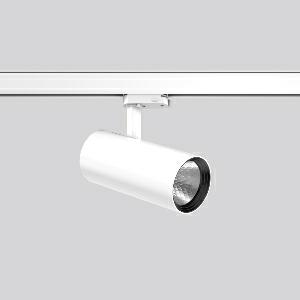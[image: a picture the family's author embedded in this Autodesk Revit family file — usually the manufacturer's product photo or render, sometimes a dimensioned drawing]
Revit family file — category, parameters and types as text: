
# Revit family: deecos_s_mini_742196_002_3_76_8a93
name_source: partatom
category: Lighting Fixtures
units: mm (PartAtom-declared; Revit-internal decimal feet)

## family parameters
Cut with Voids When Loaded = No
Host = Face
Light Source = No
Part Type = Normal
Room Calculation Point = No
Round Connector Dimension = Use Diameter
Shared = No

## types (1)
- DEECOS S mini (1 x LED Modul 935, 2500 lm, 3500)
    Apparent Load = 20 VA
    Approval mark = CE
    CIE Flux Codes = 99 100 100 100 100
    Color Rendering = 92
    Color Temperature = 3500
    Default Elevation = 1800 mm
    Description = Series: DEECOS S mini
LED surface-mounted projector in modern design with no visible cooling ribs. Housing: die-cast aluminium, powder-coated. Rotation range: 356°. Swivel range: 90°. Black plastic ring and recessed LED to prevent glare from the side. Optical assembly with reflector made of MIRO-Silver with 98% total light reflection for outstanding efficiency - can be changed without tools. Best colour rendering index Ra>90. With adapter for RZB 3-circuit DALI tracks. Suitable for Track on ceiling, Wall track. High quality converter without flickering and stroboscopic effect. The following accessories can be mounted without use of tools: interchangeable lenses, decorative glasses, honeycomb louvre, clear and frosted diffusers, white interchangeable plastic ring. 
Colour: traffic white, matt (RAL 9016)
Diameter: 87 mm
Height: 214 mm
Lamp: LED
Socket: without socket
Colour temperature: 3500K
Colour rendering index (CRI): 92
System power: 20 W
Rated luminous flux: 2500 lm
Luminous efficiency: 125 lm/W
Control gear: Converter, dimmable, DALI
Protection class: I
Type of protection: IP 20
    Height = 214 mm
    Lamp = 1 x LED Modul 935
    Lamp Light Flux = 2500 lm
    Lamp count = 1
    Length = 87 mm
    Lifetime = 50000 h
    Luminous efficacy = 125 lm/W
    Manufacturer = RZB
    ModVariant = No
    Model = 742196.002.3.76
    Mounting Place = Ceiling
    Mounting Type = Rail mounted
    Number of Poles = 1
    OnlyDefault = Yes
    Power Factor = 1
    Product Name = DEECOS S mini
    Product group = Track mounted projectors
    ProductGroupID = 301
    Protection Class = Protection class I
    Protection Degree = IP 20
    RLX_Detail_Level = 1
    RLX_Emergency_Light_Flux = 0 lm
    RLX_Emergency_Type = 0
    RLX_Emergency_Type_DB = No
    RlxData = <blob elided: 35369 chars, md5=3188082f>
    Socket = socket
    Standby Power = 0 W
    System Light Flux = 2500 lm
    System Power = 20 W
    Type Comments = Product without accessories
    Type Image = 741926.002.jpg
    URL = http://relux.com
    VarID = ---
    Voltage = 230 V
    Voltage Range = 220-240 V
    Weight = 0.00 kg
    Width = 0 mm  [stored 0 ft]

note: [stored X ft] marks values corroborated as IEEE doubles in the binary element streams (Revit-internal decimal feet)

## geometry (parser evidence)
native form markers: Blend x4, Sweep x11
no freeform markers — native parametric forms only
